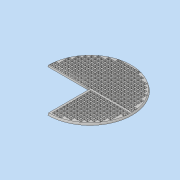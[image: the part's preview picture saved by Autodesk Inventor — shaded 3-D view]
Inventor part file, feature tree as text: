
AUTODESK INVENTOR PART (.ipt)
format: ipt  version: 2019 (Build 230136000, 136)  size: 1,906,688 bytes
history: native  units: mm
features: sketch x21, extrude x20, pattern_linear x6, other x4, projected_geometry x3, revolve x1, loft x1, shell x1, mirror x1
ambient origin geometry x8: Origin, YZ Plane, XZ Plane, XY Plane, X Axis, Y Axis, Z Axis, Center Point
bodies: Body1 (feature_tree)
feature tree (58):
  other  "полочка"
  revolve  "Вращение3"
  extrude  "Выдавливание103"  Depth=170.0mm
  sketch  "Эскиз4"
  other  "РабПлоскость1"
  sketch  "Эскиз5"
  loft  "Лофт1"
  extrude  "Выдавливание2"  Depth=17.0mm
  shell  "Оболочка1"  Thickness=4.0mm
  sketch  "Эскиз21"
  extrude  "Выдавливание16"  Depth=35.0mm
  other  "РабПлоскость7"
  sketch  "Эскиз23"
  extrude  "Выдавливание17"  TaperAngle=0.0deg  [1 undecoded]
  extrude  "Выдавливание18"  TaperAngle=0.0deg  [1 undecoded]
  extrude  "Выдавливание22"  TaperAngle=0.0deg  [1 undecoded]
  extrude  "Выдавливание24"  Depth=130.0mm TaperAngle=0.0deg
  extrude  "Выдавливание25"  Depth=5.0mm
  pattern_linear  "Прямоуг.массив1"  Spacing1=2.0mm  [1 undecoded]
  pattern_linear  "Прямоуг.массив2"  Spacing1=2.0mm  [1 undecoded]
  extrude  "Выдавливание26"  Depth=10.0mm TaperAngle=0.0deg
  pattern_linear  "Прямоуг.массив3"  Spacing1=143.802871mm  [1 undecoded]
  extrude  "Выдавливание27"  TaperAngle=0.0deg  [1 undecoded]
  pattern_linear  "Прямоуг.массив4"  Spacing1=1.0mm  [1 undecoded]
  extrude  "Выдавливание28"  Depth=30.0mm
  pattern_linear  "Прямоуг.массив5"  Spacing1=2.0mm  [1 undecoded]
  extrude  "Выдавливание29"  Depth=1.0mm TaperAngle=0.0deg
  pattern_linear  "Прямоуг.массив6"  Spacing1=14.0mm  [1 undecoded]
  mirror  "Зеркальное отражение7"
  extrude  "Выдавливание95"  Depth=14.0mm
  extrude  "Выдавливание96"  Depth=7.0mm
  extrude  "Выдавливание97"  Depth=10.0mm
  sketch  "Эскиз112"
  extrude  "Выдавливание98"  Depth=3.0mm
  extrude  "Выдавливание99"  Depth=3.0mm
  extrude  "Выдавливание100"  Depth=1.0mm TaperAngle=0.0deg
  extrude  "Выдавливание101"  Depth=14.0mm
  extrude  "Выдавливание102"  Depth=14.0mm
  sketch  "Эскиз6"
  projected_geometry  "Спроецированная петля1"
  sketch  "Эскиз26"
  sketch  "Эскиз28"
  sketch  "Эскиз29"
  sketch  "Эскиз30"
  sketch  "Эскиз31"
  sketch  "Эскиз32"
  sketch  "Эскиз33"
  sketch  "Эскиз109"
  sketch  "Эскиз110"
  sketch  "Эскиз111"
  projected_geometry  "Спроецированная петля42"
  sketch  "Эскиз114"
  projected_geometry  "Спроецированная петля43"
  sketch  "Эскиз115"
  sketch  "Эскиз116"
  sketch  "Эскиз118"
  other  "Твердое тело3"
  sketch  "Эскиз119"
note: 10 required parameter values undecoded (feature->parameter linkage not recoverable at this tier; creation-order binding heuristic only, values carry confidence <= 0.55)
